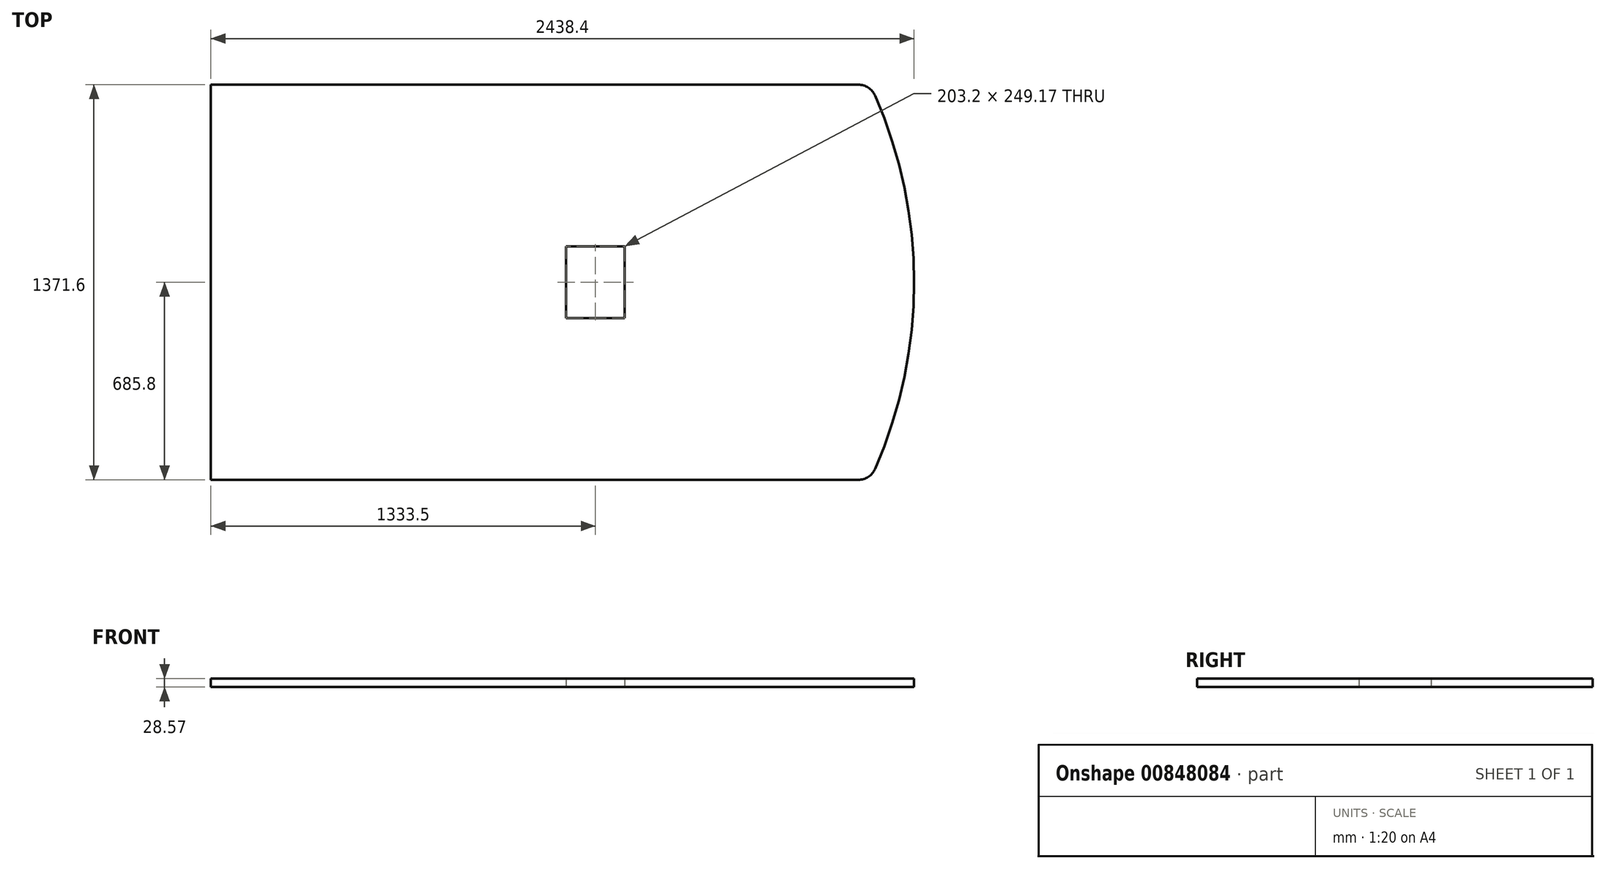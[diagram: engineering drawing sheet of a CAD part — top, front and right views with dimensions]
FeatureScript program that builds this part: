
annotation { "Feature Type Name" : "Feature", "Feature Type Description" : "" }
export const myFeature = defineFeature(function(context is Context, id is Id, definition is map)
    precondition{}
    {
        {
            var Q0;
            Q0=qCreatedBy(makeId("Top.planeOp"),FACE);
            var sketch = newSketch(context, id + "F0", { "sketchPlane" : qUnion([Q0])});
            skLineSegment(sketch, "E0.bottom", {"start": v(-1143, 685.8) * mm, "end": v(1102.02, 685.8) * mm});
            skLineSegment(sketch, "E0.top", {"start": v(-1143, -685.8) * mm, "end": v(1102.02, -685.8) * mm});
            skLineSegment(sketch, "E0.left", {"start": v(-1143, 685.8) * mm, "end": v(-1143, -685.8) * mm});
            skPoint(sketch, "E0.middle", {"position": v(0, 0) * mm});
            skLineSegment(sketch, "E1", {"start": v(1143, 0) * mm, "end": v(1295.4, 0) * mm});
            skArc(sketch, "E2", {"start": v(1160.22, -647.7) * mm, "mid": v(1295.4, 0) * mm, "end": v(1160.22, 647.7) * mm});
            skPoint(sketch, "E3.visualSharp", {"position": v(1143, 685.8) * mm});
            skArc(sketch, "E3.filletArc", {"start": v(1160.22, 647.7) * mm, "mid": v(1136.8, 675.43) * mm, "end": v(1102.02, 685.8) * mm});
            skPoint(sketch, "E4.visualSharp", {"position": v(1143, -685.8) * mm});
            skArc(sketch, "E4.filletArc", {"start": v(1102.02, -685.8) * mm, "mid": v(1136.8, -675.43) * mm, "end": v(1160.22, -647.7) * mm});
            skLineSegment(sketch, "E5", {"start": v(1143, 0) * mm, "end": v(-1143, 0) * mm});
            skLineSegment(sketch, "E6", {"start": v(1295.4, 0) * mm, "end": v(190.5, 0) * mm});
            skLineSegment(sketch, "E7.bottom", {"start": v(292.1, 124.59) * mm, "end": v(88.9, 124.59) * mm});
            skLineSegment(sketch, "E7.top", {"start": v(292.1, -124.59) * mm, "end": v(88.9, -124.59) * mm});
            skLineSegment(sketch, "E7.left", {"start": v(292.1, 124.59) * mm, "end": v(292.1, -124.59) * mm});
            skLineSegment(sketch, "E7.right", {"start": v(88.9, 124.59) * mm, "end": v(88.9, -124.59) * mm});
            skPoint(sketch, "E7.middle", {"position": v(190.5, 0) * mm});
            skSolve(sketch);
        }
        {
            var Q0;
            {var subQ2=sQuery(id+"F0.wireOp",EDGE,"bponJt8q-Vroz-T6uM-5gtj-sUBrWClouF9q");Q0=makeQuery(id+"F0.imprint","IMPRINT",FACE,{"disambiguationData":[TD([[makeQuery(id+"F0.imprint","IMPRINT",EDGE,{"derivedFrom":subQ2}),1.0]])]});}
            var Q1;
            {var subQ1=sQuery(id+"F0.wireOp",EDGE,"s5ovrSA8-h5CN-1mHA-tY9A-8cbjFLr5iEL2");Q1=makeQuery(id+"F0.imprint","IMPRINT",FACE,{"disambiguationData":[TD([[makeQuery(id+"F0.imprint","IMPRINT",EDGE,{"derivedFrom":subQ1}),-1.0]])]});}
            var Q2;
            Q2=makeQuery(id+"F0.imprint","IMPRINT",FACE,{"disambiguationData":[TD([[makeQuery(id+"F0.imprint","IMPRINT",EDGE,{"derivedFrom":sQuery(id+"F0.wireOp",EDGE,"E0.bottom")}),-1.0]])]});
            var Q3;
            {var subQ0=sQuery(id+"F0.wireOp",EDGE,"E1");Q3=makeQuery(id+"F0.imprint","IMPRINT",FACE,{"disambiguationData":[TD([[makeQuery(id+"F0.imprint","IMPRINT",EDGE,{"derivedFrom":subQ0}),-1.0]])]});}
            var Q4;
            {var subQ4=sQuery(id+"F0.wireOp",EDGE,"E0.top");Q4=makeQuery(id+"F0.imprint","IMPRINT",FACE,{"disambiguationData":[TD([[makeQuery(id+"F0.imprint","IMPRINT",EDGE,{"derivedFrom":subQ4}),1.0]])]});}
            extrude(context, id + "F1", {"entities" : qUnion([Q0, Q1, Q2, Q3, Q4]), "depth" : 28.57 * mm, "offsetDistance" : 25.4 * mm});
        }
    });
